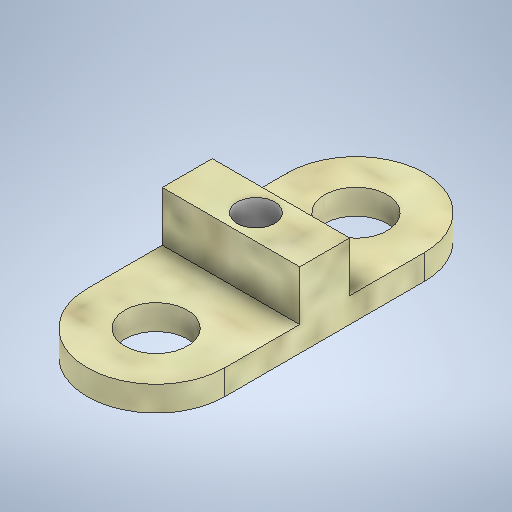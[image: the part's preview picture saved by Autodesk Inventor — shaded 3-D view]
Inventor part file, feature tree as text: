
AUTODESK INVENTOR PART (.ipt)
format: ipt  version: 2025.1 (Build 291241000, 241)  size: 340,480 bytes
history: native  units: in
note: dims shown in document units (in); Inventor stores cm internally (conversion verified against a paired STEP export)
features: extrude x3, sketch x3, projected_geometry x1, other x1
ambient origin geometry x8: Origin, YZ Plane, XZ Plane, XY Plane, X Axis, Y Axis, Z Axis, Center Point
bodies: Solid1 (feature_tree)
feature tree (8):
  extrude  "Extrusion1"  Depth=0.4331in
  extrude  "Extrusion2"  Depth=0.4331in
  extrude  "Extrusion3"  Depth=0.0787in TaperAngle=0.0deg
  sketch  "Sketch1"  dims[d0=0.4331in d1=0.6299in]
  sketch  "Sketch2"  dims[d2=0.4331in d3=0.1969in]
  sketch  "Sketch3"  dims[d4=0.1969in d5=0.0787in d6=0.0in d7=0.1575in d8=0.1575in d9=0.0in d11=0.655in d12=0.0in d15=0.1181in]
  projected_geometry  "Projected Loop1"
  other  "Finish1"
